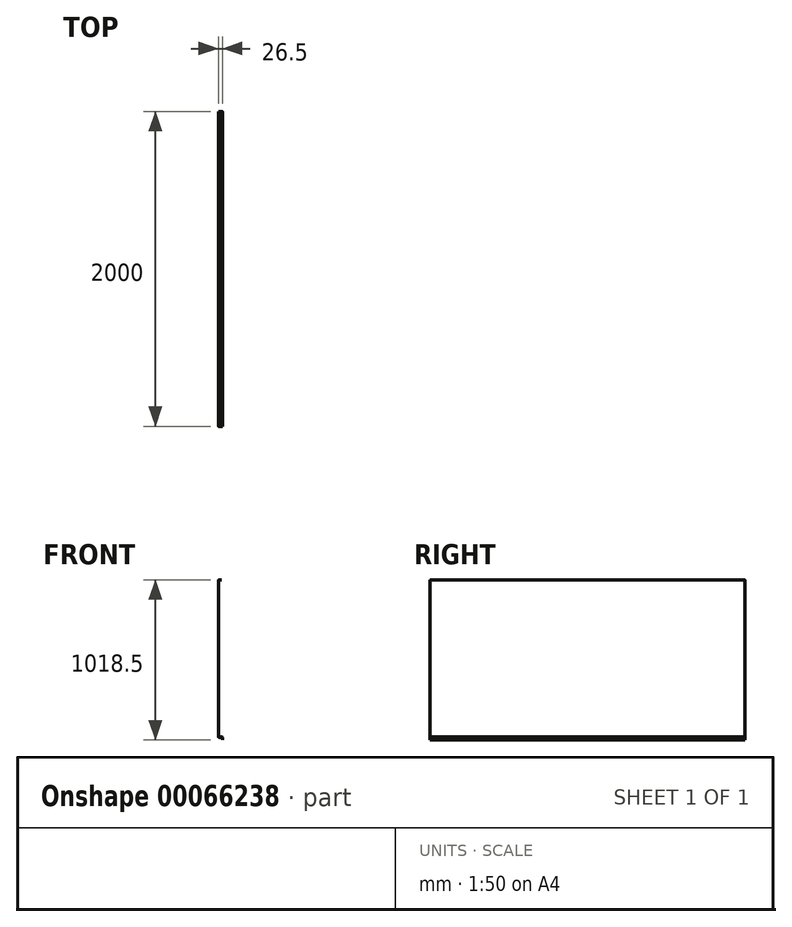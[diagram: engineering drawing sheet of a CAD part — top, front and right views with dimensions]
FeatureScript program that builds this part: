
annotation { "Feature Type Name" : "Feature", "Feature Type Description" : "" }
export const myFeature = defineFeature(function(context is Context, id is Id, definition is map)
    precondition{}
    {
        {
            var Q0;
            Q0=qCreatedBy(makeId("Front.planeOp"),FACE);
            var sketch = newSketch(context, id + "F0", { "sketchPlane" : qUnion([Q0])});
            skLineSegment(sketch, "E0", {"start": v(-15.74, -5.36) * mm, "end": v(-15.74, 10.64) * mm});
            skLineSegment(sketch, "E1", {"start": v(-19.74, 14.64) * mm, "end": v(-38.24, 14.64) * mm});
            skLineSegment(sketch, "E2", {"start": v(-40.74, 17.14) * mm, "end": v(-40.74, 1009.14) * mm});
            skLineSegment(sketch, "E3", {"start": v(-38.24, 1011.64) * mm, "end": v(-22.24, 1011.64) * mm});
            skLineSegment(sketch, "E4.0", {"start": v(-17.24, -5.36) * mm, "end": v(-17.24, 10.64) * mm});
            skLineSegment(sketch, "E5.0", {"start": v(-19.74, 13.14) * mm, "end": v(-38.24, 13.14) * mm});
            skLineSegment(sketch, "E6.0", {"start": v(-42.24, 17.14) * mm, "end": v(-42.24, 1009.14) * mm});
            skLineSegment(sketch, "E7.0", {"start": v(-38.24, 1013.14) * mm, "end": v(-22.24, 1013.14) * mm});
            skLineSegment(sketch, "E8", {"start": v(-17.24, -5.36) * mm, "end": v(-15.74, -5.36) * mm});
            skLineSegment(sketch, "E9", {"start": v(-22.24, 1011.64) * mm, "end": v(-22.24, 1013.14) * mm});
            skPoint(sketch, "E10.visualSharp", {"position": v(-40.74, 1011.64) * mm});
            skArc(sketch, "E10.filletArc", {"start": v(-38.24, 1011.64) * mm, "mid": v(-40.01, 1010.9) * mm, "end": v(-40.74, 1009.14) * mm});
            skPoint(sketch, "E11.visualSharp", {"position": v(-40.74, 14.64) * mm});
            skArc(sketch, "E11.filletArc", {"start": v(-40.74, 17.14) * mm, "mid": v(-40.01, 15.37) * mm, "end": v(-38.24, 14.64) * mm});
            skArc(sketch, "E12.filletArc", {"start": v(-17.24, 10.64) * mm, "mid": v(-17.98, 12.4) * mm, "end": v(-19.74, 13.14) * mm});
            skArc(sketch, "E13.filletArc", {"start": v(-38.24, 1013.14) * mm, "mid": v(-41.07, 1011.97) * mm, "end": v(-42.24, 1009.14) * mm});
            skArc(sketch, "E14.filletArc", {"start": v(-42.24, 17.14) * mm, "mid": v(-41.07, 14.31) * mm, "end": v(-38.24, 13.14) * mm});
            skPoint(sketch, "E15.visualSharp", {"position": v(-15.74, 14.64) * mm});
            skArc(sketch, "E15.filletArc", {"start": v(-15.74, 10.64) * mm, "mid": v(-16.91, 13.47) * mm, "end": v(-19.74, 14.64) * mm});
            skSolve(sketch);
        }
        {
            var Q0;
            Q0=makeQuery(id+"F0.imprint","IMPRINT",FACE,{"disambiguationData":[TD([[makeQuery(id+"F0.imprint","IMPRINT",EDGE,{"derivedFrom":sQuery(id+"F0.wireOp",EDGE,"E0")}),1.0]])]});
            extrude(context, id + "F1", {"entities" : qUnion([Q0]), "depth" : 2000 * mm});
        }
    });
